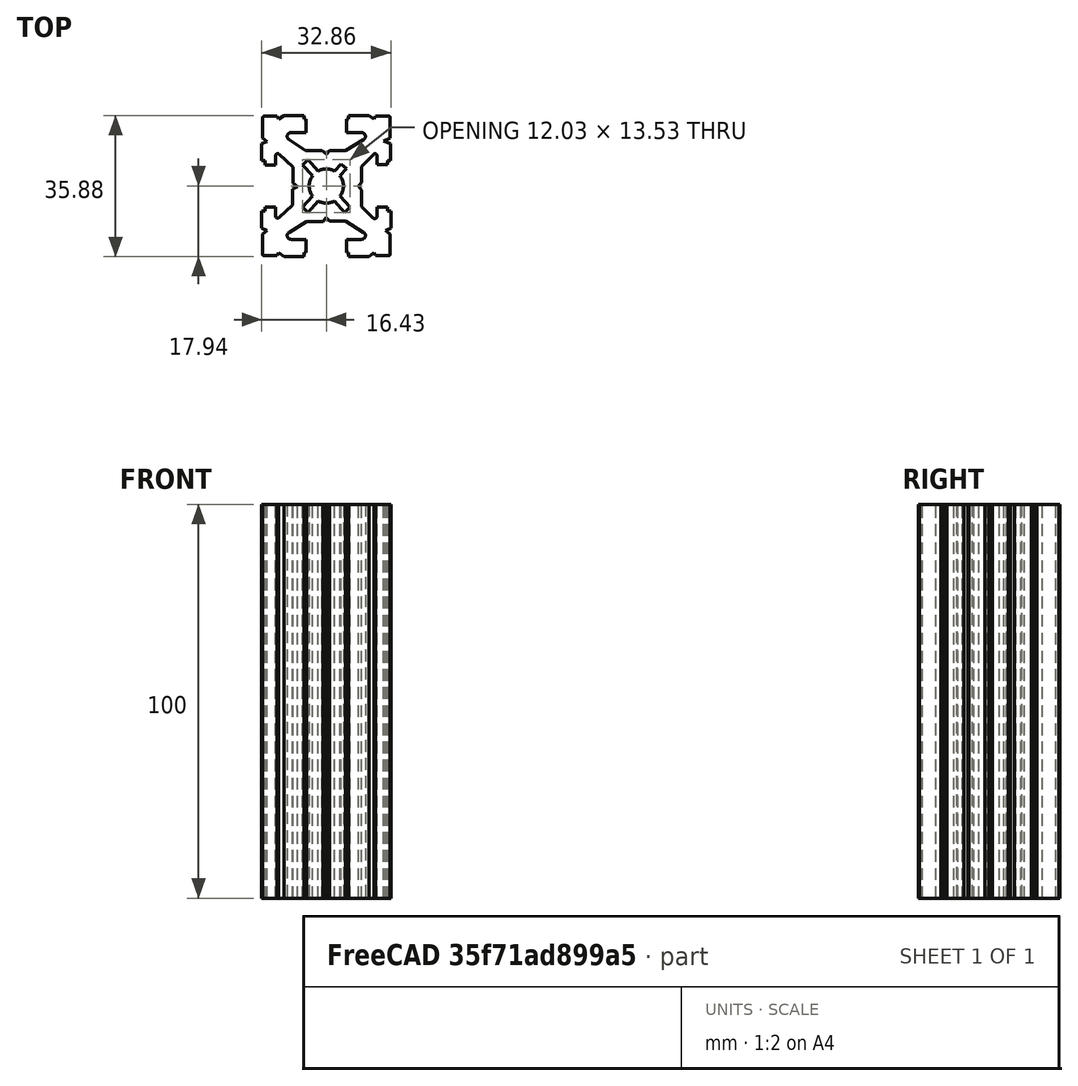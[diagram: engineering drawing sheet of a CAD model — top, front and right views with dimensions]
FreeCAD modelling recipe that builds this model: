
FCSTD DOCUMENT  (FreeCAD 0.17R13509 (Git))
Label: Profile Bosh 30x30mm
License: Creative Commons Attribution 3.0
LicenseURL: https://creativecommons.org/licenses/by/3.0/
objects: Sketcher::SketchObject×2, PartDesign::Pad×1, PartDesign::Body×1, App::Part×1
note: 5 computed .brp shape members not serialized (recipe doc carries the construction recipe); baked Part::Feature solids carry a one-line shape summary decoded from their .brp

FEATURE [Sketcher::SketchObject] Sketch
  sketch-geometry (116):
    g0: BSplineCurve PolesCount=2 KnotsCount=2 Degree=1 IsPeriodic=0
    g1: BSplineCurve PolesCount=2 KnotsCount=2 Degree=1 IsPeriodic=0
    g2: BSplineCurve PolesCount=2 KnotsCount=2 Degree=1 IsPeriodic=0
    g3: BSplineCurve PolesCount=3 KnotsCount=2 Degree=2 IsPeriodic=0
    g4: BSplineCurve PolesCount=3 KnotsCount=2 Degree=2 IsPeriodic=0
    g5: BSplineCurve PolesCount=3 KnotsCount=2 Degree=2 IsPeriodic=0
    g6: BSplineCurve PolesCount=3 KnotsCount=2 Degree=2 IsPeriodic=0
    g7: BSplineCurve PolesCount=3 KnotsCount=2 Degree=2 IsPeriodic=0
    g8: BSplineCurve PolesCount=3 KnotsCount=2 Degree=2 IsPeriodic=0
    g9: BSplineCurve PolesCount=3 KnotsCount=2 Degree=2 IsPeriodic=0
    g10: BSplineCurve PolesCount=3 KnotsCount=2 Degree=2 IsPeriodic=0
    g11: BSplineCurve PolesCount=2 KnotsCount=2 Degree=1 IsPeriodic=0
    g12: BSplineCurve PolesCount=2 KnotsCount=2 Degree=1 IsPeriodic=0
    g13: BSplineCurve PolesCount=2 KnotsCount=2 Degree=1 IsPeriodic=0
    g14: BSplineCurve PolesCount=2 KnotsCount=2 Degree=1 IsPeriodic=0
    g15: BSplineCurve PolesCount=2 KnotsCount=2 Degree=1 IsPeriodic=0
    g16: BSplineCurve PolesCount=2 KnotsCount=2 Degree=1 IsPeriodic=0
    g17: BSplineCurve PolesCount=2 KnotsCount=2 Degree=1 IsPeriodic=0
    g18: BSplineCurve PolesCount=2 KnotsCount=2 Degree=1 IsPeriodic=0
    g19: BSplineCurve PolesCount=2 KnotsCount=2 Degree=1 IsPeriodic=0
    g20: BSplineCurve PolesCount=2 KnotsCount=2 Degree=1 IsPeriodic=0
    g21: BSplineCurve PolesCount=2 KnotsCount=2 Degree=1 IsPeriodic=0
    g22: BSplineCurve PolesCount=2 KnotsCount=2 Degree=1 IsPeriodic=0
    g23: BSplineCurve PolesCount=2 KnotsCount=2 Degree=1 IsPeriodic=0
    g24: BSplineCurve PolesCount=2 KnotsCount=2 Degree=1 IsPeriodic=0
    g25: BSplineCurve PolesCount=2 KnotsCount=2 Degree=1 IsPeriodic=0
    g26: BSplineCurve PolesCount=2 KnotsCount=2 Degree=1 IsPeriodic=0
    g27: BSplineCurve PolesCount=2 KnotsCount=2 Degree=1 IsPeriodic=0
    g28: BSplineCurve PolesCount=2 KnotsCount=2 Degree=1 IsPeriodic=0
    g29: BSplineCurve PolesCount=2 KnotsCount=2 Degree=1 IsPeriodic=0
    g30: BSplineCurve PolesCount=2 KnotsCount=2 Degree=1 IsPeriodic=0
    g31: BSplineCurve PolesCount=2 KnotsCount=2 Degree=1 IsPeriodic=0
    g32: BSplineCurve PolesCount=2 KnotsCount=2 Degree=1 IsPeriodic=0
    g33: BSplineCurve PolesCount=2 KnotsCount=2 Degree=1 IsPeriodic=0
    g34: BSplineCurve PolesCount=2 KnotsCount=2 Degree=1 IsPeriodic=0
    g35: BSplineCurve PolesCount=2 KnotsCount=2 Degree=1 IsPeriodic=0
    g36: BSplineCurve PolesCount=2 KnotsCount=2 Degree=1 IsPeriodic=0
    g37: BSplineCurve PolesCount=2 KnotsCount=2 Degree=1 IsPeriodic=0
    g38: BSplineCurve PolesCount=2 KnotsCount=2 Degree=1 IsPeriodic=0
    g39: BSplineCurve PolesCount=2 KnotsCount=2 Degree=1 IsPeriodic=0
    g40: BSplineCurve PolesCount=2 KnotsCount=2 Degree=1 IsPeriodic=0
    g41: BSplineCurve PolesCount=2 KnotsCount=2 Degree=1 IsPeriodic=0
    g42: BSplineCurve PolesCount=2 KnotsCount=2 Degree=1 IsPeriodic=0
    g43: BSplineCurve PolesCount=2 KnotsCount=2 Degree=1 IsPeriodic=0
    g44: BSplineCurve PolesCount=3 KnotsCount=2 Degree=2 IsPeriodic=0
    g45: BSplineCurve PolesCount=2 KnotsCount=2 Degree=1 IsPeriodic=0
    g46: BSplineCurve PolesCount=2 KnotsCount=2 Degree=1 IsPeriodic=0
    g47: BSplineCurve PolesCount=2 KnotsCount=2 Degree=1 IsPeriodic=0
    g48: BSplineCurve PolesCount=2 KnotsCount=2 Degree=1 IsPeriodic=0
    g49: BSplineCurve PolesCount=3 KnotsCount=2 Degree=2 IsPeriodic=0
    g50: BSplineCurve PolesCount=2 KnotsCount=2 Degree=1 IsPeriodic=0
    g51: BSplineCurve PolesCount=3 KnotsCount=2 Degree=2 IsPeriodic=0
    g52: BSplineCurve PolesCount=3 KnotsCount=2 Degree=2 IsPeriodic=0
    g53: BSplineCurve PolesCount=3 KnotsCount=2 Degree=2 IsPeriodic=0
    g54: BSplineCurve PolesCount=2 KnotsCount=2 Degree=1 IsPeriodic=0
    g55: BSplineCurve PolesCount=2 KnotsCount=2 Degree=1 IsPeriodic=0
    g56: BSplineCurve PolesCount=2 KnotsCount=2 Degree=1 IsPeriodic=0
    g57: BSplineCurve PolesCount=2 KnotsCount=2 Degree=1 IsPeriodic=0
    g58: BSplineCurve PolesCount=3 KnotsCount=2 Degree=2 IsPeriodic=0
    g59: BSplineCurve PolesCount=3 KnotsCount=2 Degree=2 IsPeriodic=0
    g60: BSplineCurve PolesCount=3 KnotsCount=2 Degree=2 IsPeriodic=0
    g61: BSplineCurve PolesCount=2 KnotsCount=2 Degree=1 IsPeriodic=0
    g62: BSplineCurve PolesCount=2 KnotsCount=2 Degree=1 IsPeriodic=0
    g63: BSplineCurve PolesCount=2 KnotsCount=2 Degree=1 IsPeriodic=0
    g64: BSplineCurve PolesCount=2 KnotsCount=2 Degree=1 IsPeriodic=0
    g65: BSplineCurve PolesCount=2 KnotsCount=2 Degree=1 IsPeriodic=0
    g66: BSplineCurve PolesCount=2 KnotsCount=2 Degree=1 IsPeriodic=0
    g67: BSplineCurve PolesCount=2 KnotsCount=2 Degree=1 IsPeriodic=0
    g68: BSplineCurve PolesCount=2 KnotsCount=2 Degree=1 IsPeriodic=0
    g69: BSplineCurve PolesCount=2 KnotsCount=2 Degree=1 IsPeriodic=0
    g70: BSplineCurve PolesCount=2 KnotsCount=2 Degree=1 IsPeriodic=0
    g71: BSplineCurve PolesCount=2 KnotsCount=2 Degree=1 IsPeriodic=0
    g72: BSplineCurve PolesCount=2 KnotsCount=2 Degree=1 IsPeriodic=0
    g73: BSplineCurve PolesCount=2 KnotsCount=2 Degree=1 IsPeriodic=0
    g74: BSplineCurve PolesCount=2 KnotsCount=2 Degree=1 IsPeriodic=0
    g75: BSplineCurve PolesCount=2 KnotsCount=2 Degree=1 IsPeriodic=0
    g76: BSplineCurve PolesCount=2 KnotsCount=2 Degree=1 IsPeriodic=0
    g77: BSplineCurve PolesCount=2 KnotsCount=2 Degree=1 IsPeriodic=0
    g78: BSplineCurve PolesCount=2 KnotsCount=2 Degree=1 IsPeriodic=0
    g79: BSplineCurve PolesCount=2 KnotsCount=2 Degree=1 IsPeriodic=0
    g80: BSplineCurve PolesCount=2 KnotsCount=2 Degree=1 IsPeriodic=0
    g81: BSplineCurve PolesCount=2 KnotsCount=2 Degree=1 IsPeriodic=0
    g82: BSplineCurve PolesCount=2 KnotsCount=2 Degree=1 IsPeriodic=0
    g83: BSplineCurve PolesCount=2 KnotsCount=2 Degree=1 IsPeriodic=0
    g84: BSplineCurve PolesCount=2 KnotsCount=2 Degree=1 IsPeriodic=0
    g85: BSplineCurve PolesCount=2 KnotsCount=2 Degree=1 IsPeriodic=0
    g86: BSplineCurve PolesCount=2 KnotsCount=2 Degree=1 IsPeriodic=0
    g87: BSplineCurve PolesCount=2 KnotsCount=2 Degree=1 IsPeriodic=0
    g88: BSplineCurve PolesCount=2 KnotsCount=2 Degree=1 IsPeriodic=0
    g89: BSplineCurve PolesCount=2 KnotsCount=2 Degree=1 IsPeriodic=0
    g90: BSplineCurve PolesCount=2 KnotsCount=2 Degree=1 IsPeriodic=0
    g91: BSplineCurve PolesCount=2 KnotsCount=2 Degree=1 IsPeriodic=0
    g92: BSplineCurve PolesCount=2 KnotsCount=2 Degree=1 IsPeriodic=0
    g93: BSplineCurve PolesCount=2 KnotsCount=2 Degree=1 IsPeriodic=0
    g94: BSplineCurve PolesCount=2 KnotsCount=2 Degree=1 IsPeriodic=0
    g95: BSplineCurve PolesCount=2 KnotsCount=2 Degree=1 IsPeriodic=0
    g96: BSplineCurve PolesCount=2 KnotsCount=2 Degree=1 IsPeriodic=0
    g97: BSplineCurve PolesCount=2 KnotsCount=2 Degree=1 IsPeriodic=0
    g98: BSplineCurve PolesCount=2 KnotsCount=2 Degree=1 IsPeriodic=0
    g99: BSplineCurve PolesCount=2 KnotsCount=2 Degree=1 IsPeriodic=0
    g100: BSplineCurve PolesCount=2 KnotsCount=2 Degree=1 IsPeriodic=0
    g101: BSplineCurve PolesCount=2 KnotsCount=2 Degree=1 IsPeriodic=0
    g102: BSplineCurve PolesCount=2 KnotsCount=2 Degree=1 IsPeriodic=0
    g103: BSplineCurve PolesCount=2 KnotsCount=2 Degree=1 IsPeriodic=0
    g104: BSplineCurve PolesCount=2 KnotsCount=2 Degree=1 IsPeriodic=0
    g105: BSplineCurve PolesCount=2 KnotsCount=2 Degree=1 IsPeriodic=0
    g106: BSplineCurve PolesCount=2 KnotsCount=2 Degree=1 IsPeriodic=0
    g107: BSplineCurve PolesCount=2 KnotsCount=2 Degree=1 IsPeriodic=0
    g108: BSplineCurve PolesCount=2 KnotsCount=2 Degree=1 IsPeriodic=0
    g109: BSplineCurve PolesCount=2 KnotsCount=2 Degree=1 IsPeriodic=0
    g110: BSplineCurve PolesCount=2 KnotsCount=2 Degree=1 IsPeriodic=0
    g111: BSplineCurve PolesCount=2 KnotsCount=2 Degree=1 IsPeriodic=0
    g112: BSplineCurve PolesCount=2 KnotsCount=2 Degree=1 IsPeriodic=0
    g113: BSplineCurve PolesCount=2 KnotsCount=2 Degree=1 IsPeriodic=0
    g114: BSplineCurve PolesCount=2 KnotsCount=2 Degree=1 IsPeriodic=0
    g115: BSplineCurve PolesCount=2 KnotsCount=2 Degree=1 IsPeriodic=0
FEATURE [Sketcher::SketchObject] Sketch001
  MapMode = 5
  Support = -> [XY_Plane001]
  sketch-geometry (121):
    g0: LineSegment [constr] StartX=0 StartY=0 StartZ=0 EndX=0 EndY=8.13256 EndZ=0
    g1: LineSegment [constr] StartX=8.13256 StartY=0 StartZ=0 EndX=0 EndY=0 EndZ=0
    g2: LineSegment StartX=0 StartY=8.13256 StartZ=0 EndX=0.863984 EndY=8.96505 EndZ=0
    g3: LineSegment StartX=0.863984 StartY=8.96505 StartZ=0 EndX=4.93425 EndY=8.96505 EndZ=0
    g4: LineSegment StartX=4.93425 StartY=8.96505 StartZ=0 EndX=9.48637 EndY=11.797 EndZ=0
    g5: LineSegment StartX=8.98459 StartY=13.5535 StartZ=0 EndX=5.15812 EndY=13.5535 EndZ=0
    g6: LineSegment StartX=5.15812 StartY=13.5535 StartZ=0 EndX=5.15812 EndY=16.9407 EndZ=0
    g7: LineSegment StartX=5.15812 StartY=16.9407 StartZ=0 EndX=5.6531 EndY=16.9407 EndZ=0
    g8: LineSegment StartX=5.6531 StartY=16.9407 StartZ=0 EndX=5.6531 EndY=17.9363 EndZ=0
    g9: LineSegment StartX=5.6531 StartY=17.9363 StartZ=0 EndX=10.7923 EndY=17.9363 EndZ=0
    g10: LineSegment StartX=10.7923 StartY=17.9363 StartZ=0 EndX=12.0719 EndY=16.9647 EndZ=0
    g11: LineSegment StartX=12.0719 StartY=16.9647 StartZ=0 EndX=12.5221 EndY=17.7592 EndZ=0
    g12: LineSegment StartX=12.5221 StartY=17.7592 StartZ=0 EndX=15.8708 EndY=17.7592 EndZ=0
    g13: LineSegment StartX=16.246 StartY=17.384 StartZ=0 EndX=16.246 EndY=12.1724 EndZ=0
    g14: LineSegment StartX=16.246 StartY=12.1724 StartZ=0 EndX=14.4892 EndY=11.3845 EndZ=0
    g15: LineSegment StartX=14.4892 StartY=11.3845 StartZ=0 EndX=16.2567 EndY=10.735 EndZ=0
    g16: LineSegment StartX=16.2567 StartY=10.735 StartZ=0 EndX=16.2567 EndY=6.42108 EndZ=0
    g17: LineSegment StartX=16.2567 StartY=6.42108 StartZ=0 EndX=15.6194 EndY=6.42108 EndZ=0
    g18: ArcOfCircle CenterX=15.8708 CenterY=17.384 CenterZ=0 NormalX=0 NormalY=0 NormalZ=1 AngleXU=0 Radius=0.375206 StartAngle=0 EndAngle=1.5708
    g19: ArcOfCircle CenterX=12.38 CenterY=7.66792 CenterZ=0 NormalX=0 NormalY=0 NormalZ=1 AngleXU=0 Radius=0.511001 StartAngle=0 EndAngle=2.35619
    g20: ArcOfCircle CenterX=8.98459 CenterY=12.6036 CenterZ=0 NormalX=0 NormalY=0 NormalZ=1 AngleXU=0 Radius=0.949916 StartAngle=5.26891 EndAngle=7.85398
    g21: LineSegment StartX=15.6194 StartY=6.42108 StartZ=0 EndX=15.6194 EndY=5.37886 EndZ=0
    g22: LineSegment StartX=15.6194 StartY=5.37886 StartZ=0 EndX=12.891 EndY=5.37886 EndZ=0
    g23: LineSegment StartX=12.891 StartY=5.37886 StartZ=0 EndX=12.891 EndY=7.66792 EndZ=0
    g24: LineSegment StartX=12.0187 StartY=8.02925 StartZ=0 EndX=8.94375 EndY=4.95429 EndZ=0
    g25: LineSegment StartX=8.94375 StartY=4.95429 StartZ=0 EndX=8.94375 EndY=0.884017 EndZ=0
    g26: LineSegment StartX=8.94375 StartY=0.884017 StartZ=0 EndX=8.13256 EndY=0 EndZ=0
    g27: ArcOfCircle CenterX=0 CenterY=0 CenterZ=0 NormalX=0 NormalY=0 NormalZ=1 AngleXU=0 Radius=4.34461 StartAngle=1.06729 EndAngle=2.0743
    g28: LineSegment StartX=-2.09626 StartY=3.80544 StartZ=0 EndX=-4.58638 EndY=6.76319 EndZ=0
    g29: LineSegment StartX=-4.58638 StartY=6.76319 StartZ=0 EndX=-6.01301 EndY=5.3625 EndZ=0
    g30: LineSegment StartX=-6.01301 StartY=5.3625 StartZ=0 EndX=-3.47101 EndY=2.61299 EndZ=0
    g31: LineSegment StartX=2.09626 StartY=3.80544 StartZ=0 EndX=3.70713 EndY=5.62355 EndZ=0
    g32: LineSegment StartX=3.70713 StartY=5.62355 StartZ=0 EndX=5.08583 EndY=4.45696 EndZ=0
    g33: LineSegment StartX=5.08583 StartY=4.45696 StartZ=0 EndX=3.47101 EndY=2.61299 EndZ=0
    g34: LineSegment StartX=2.09626 StartY=-3.80544 StartZ=0 EndX=4.58638 EndY=-6.76319 EndZ=0
    g35: LineSegment StartX=4.58638 StartY=-6.76319 StartZ=0 EndX=6.01301 EndY=-5.3625 EndZ=0
    g36: LineSegment StartX=6.01301 StartY=-5.3625 StartZ=0 EndX=3.47101 EndY=-2.61299 EndZ=0
    g37: LineSegment StartX=-2.09626 StartY=-3.80544 StartZ=0 EndX=-4.58638 EndY=-6.76319 EndZ=0
    g38: LineSegment StartX=-6.01301 StartY=-5.3625 StartZ=0 EndX=-3.47101 EndY=-2.61299 EndZ=0
    g39: LineSegment StartX=-4.58638 StartY=-6.76319 StartZ=0 EndX=-6.01301 EndY=-5.3625 EndZ=0
    g40: ArcOfCircle CenterX=0 CenterY=0 CenterZ=0 NormalX=0 NormalY=0 NormalZ=1 AngleXU=0 Radius=4.34461 StartAngle=2.4963 EndAngle=3.78689
    g41: ArcOfCircle CenterX=0 CenterY=0 CenterZ=0 NormalX=0 NormalY=0 NormalZ=1 AngleXU=0 Radius=4.34461 StartAngle=4.20889 EndAngle=5.21589
    g42: ArcOfCircle CenterX=0 CenterY=0 CenterZ=0 NormalX=0 NormalY=0 NormalZ=1 AngleXU=0 Radius=4.34461 StartAngle=5.63789 EndAngle=6.92848
    g43: LineSegment [constr] StartX=8.94375 StartY=4.95429 StartZ=0 EndX=10.2141 EndY=4.95429 EndZ=0
    g44: LineSegment StartX=0 StartY=8.13256 StartZ=0 EndX=-1.12485 EndY=9.01316 EndZ=0
    g45: LineSegment StartX=-1.12485 StartY=9.01316 StartZ=0 EndX=-5.23766 EndY=9.01316 EndZ=0
    g46: LineSegment StartX=-5.23766 StartY=9.01316 StartZ=0 EndX=-9.50558 EndY=11.8091 EndZ=0
    g47: LineSegment StartX=-8.98499 StartY=13.5537 StartZ=0 EndX=-5.15812 EndY=13.5537 EndZ=0
    g48: LineSegment StartX=-5.15812 StartY=13.5537 StartZ=0 EndX=-5.15812 EndY=16.9407 EndZ=0
    g49: LineSegment StartX=-5.15812 StartY=16.9407 StartZ=0 EndX=-5.6531 EndY=16.9407 EndZ=0
    g50: LineSegment StartX=-5.6531 StartY=16.9407 StartZ=0 EndX=-5.6531 EndY=17.9363 EndZ=0
    g51: LineSegment StartX=-5.6531 StartY=17.9363 StartZ=0 EndX=-10.7923 EndY=17.9363 EndZ=0
    g52: LineSegment StartX=-10.7923 StartY=17.9363 StartZ=0 EndX=-12.0719 EndY=16.9647 EndZ=0
    g53: LineSegment StartX=-12.0719 StartY=16.9647 StartZ=0 EndX=-12.5221 EndY=17.7251 EndZ=0
    g54: LineSegment StartX=-12.5221 StartY=17.7251 StartZ=0 EndX=-15.8282 EndY=17.7251 EndZ=0
    g55: LineSegment StartX=-16.1524 StartY=17.401 StartZ=0 EndX=-16.1524 EndY=12.1805 EndZ=0
    g56: LineSegment StartX=-16.1524 StartY=12.1805 StartZ=0 EndX=-14.9921 EndY=11.3367 EndZ=0
    g57: LineSegment StartX=-14.9921 StartY=11.3367 StartZ=0 EndX=-16.4328 EndY=10.7136 EndZ=0
    g58: LineSegment StartX=-16.4328 StartY=10.7136 StartZ=0 EndX=-16.4328 EndY=6.42108 EndZ=0
    g59: LineSegment StartX=-16.4328 StartY=6.42108 StartZ=0 EndX=-15.6194 EndY=6.42108 EndZ=0
    g60: ArcOfCircle CenterX=-15.8282 CenterY=17.401 CenterZ=0 NormalX=0 NormalY=0 NormalZ=1 AngleXU=0 Radius=0.324122 StartAngle=1.5708 EndAngle=3.14159
    g61: ArcOfCircle CenterX=-8.98499 CenterY=12.6037 CenterZ=0 NormalX=0 NormalY=0 NormalZ=1 AngleXU=0 Radius=0.949992 StartAngle=1.5708 EndAngle=4.13243
    g62: LineSegment StartX=-15.6194 StartY=6.42108 StartZ=0 EndX=-15.6194 EndY=5.3545 EndZ=0
    g63: LineSegment StartX=-15.6194 StartY=5.3545 StartZ=0 EndX=-12.8911 EndY=5.3545 EndZ=0
    g64: ArcOfCircle CenterX=-12.3588 CenterY=7.67266 CenterZ=0 NormalX=0 NormalY=0 NormalZ=1 AngleXU=0 Radius=0.532302 StartAngle=0.822691 EndAngle=3.14117
    g65: LineSegment StartX=-11.9967 StartY=8.06282 StartZ=0 EndX=-8.50501 EndY=4.82235 EndZ=0
    g66: LineSegment StartX=-8.50501 StartY=4.82235 StartZ=0 EndX=-8.50501 EndY=0.709539 EndZ=0
    g67: LineSegment StartX=-8.50501 StartY=0.709539 StartZ=0 EndX=-7.362 EndY=-0.147361 EndZ=0
    g68: LineSegment [constr] StartX=-0.0366578 StartY=0 StartZ=0 EndX=-0.0366578 EndY=-7.97192 EndZ=0
    g69: LineSegment StartX=-0.0366578 StartY=-7.97192 StartZ=0 EndX=0.851967 EndY=-8.95417 EndZ=0
    g70: LineSegment StartX=0.851967 StartY=-8.95417 StartZ=0 EndX=4.95077 EndY=-8.95417 EndZ=0
    g71: LineSegment StartX=4.95077 StartY=-8.95417 StartZ=0 EndX=9.48868 EndY=-11.7973 EndZ=0
    g72: LineSegment StartX=8.98403 StartY=-13.5532 StartZ=0 EndX=5.15812 EndY=-13.5532 EndZ=0
    g73: LineSegment StartX=5.15812 StartY=-13.5532 StartZ=0 EndX=5.15812 EndY=-16.9407 EndZ=0
    g74: LineSegment StartX=5.15812 StartY=-16.9407 StartZ=0 EndX=5.6531 EndY=-16.9407 EndZ=0
    g75: LineSegment StartX=5.6531 StartY=-16.9407 StartZ=0 EndX=5.6531 EndY=-17.9363 EndZ=0
    g76: LineSegment StartX=5.6531 StartY=-17.9363 StartZ=0 EndX=10.7923 EndY=-17.9363 EndZ=0
    g77: LineSegment StartX=10.7923 StartY=-17.9363 StartZ=0 EndX=12.0719 EndY=-16.9647 EndZ=0
    g78: LineSegment StartX=12.0719 StartY=-16.9647 StartZ=0 EndX=12.5221 EndY=-17.7251 EndZ=0
    g79: LineSegment StartX=12.5221 StartY=-17.7251 StartZ=0 EndX=15.8282 EndY=-17.7251 EndZ=0
    g80: LineSegment StartX=16.1524 StartY=-17.401 StartZ=0 EndX=16.1524 EndY=-12.1805 EndZ=0
    g81: LineSegment StartX=16.1524 StartY=-12.1805 StartZ=0 EndX=14.9921 EndY=-11.3367 EndZ=0
    g82: LineSegment StartX=14.9921 StartY=-11.3367 StartZ=0 EndX=16.4328 EndY=-10.7136 EndZ=0
    g83: LineSegment StartX=16.4328 StartY=-10.7136 StartZ=0 EndX=16.4328 EndY=-6.42108 EndZ=0
    g84: ArcOfCircle CenterX=15.8282 CenterY=-17.401 CenterZ=0 NormalX=0 NormalY=0 NormalZ=1 AngleXU=0 Radius=0.324122 StartAngle=4.71239 EndAngle=6.28319
    g85: ArcOfCircle CenterX=12.2781 CenterY=-7.67162 CenterZ=0 NormalX=0 NormalY=0 NormalZ=1 AngleXU=0 Radius=0.613906 StartAngle=3.92699 EndAngle=6.28319
    g86: ArcOfCircle CenterX=8.98403 CenterY=-12.6027 CenterZ=0 NormalX=0 NormalY=0 NormalZ=1 AngleXU=0 Radius=0.950502 StartAngle=4.71239 EndAngle=7.29429
    g87: LineSegment StartX=12.892 StartY=-5.37886 StartZ=0 EndX=12.892 EndY=-7.67162 EndZ=0
    g88: LineSegment StartX=11.844 StartY=-8.10572 StartZ=0 EndX=8.9097 EndY=-5.17142 EndZ=0
    g89: LineSegment StartX=-0.0366578 StartY=-7.97192 StartZ=0 EndX=-0.845387 EndY=-8.98483 EndZ=0
    g90: LineSegment StartX=-0.845387 StartY=-8.98483 StartZ=0 EndX=-4.96492 EndY=-8.98483 EndZ=0
    g91: LineSegment StartX=-4.96492 StartY=-8.98483 StartZ=0 EndX=-9.48593 EndY=-11.7955 EndZ=0
    g92: LineSegment StartX=-8.98406 StartY=-13.5533 StartZ=0 EndX=-5.15812 EndY=-13.5533 EndZ=0
    g93: LineSegment StartX=-5.15812 StartY=-13.5533 StartZ=0 EndX=-5.15812 EndY=-16.9407 EndZ=0
    g94: LineSegment StartX=-5.15812 StartY=-16.9407 StartZ=0 EndX=-5.6531 EndY=-16.9407 EndZ=0
    g95: LineSegment StartX=-5.6531 StartY=-16.9407 StartZ=0 EndX=-5.6531 EndY=-17.9363 EndZ=0
    g96: LineSegment StartX=-5.6531 StartY=-17.9363 StartZ=0 EndX=-10.7923 EndY=-17.9363 EndZ=0
    g97: LineSegment StartX=-10.7923 StartY=-17.9363 StartZ=0 EndX=-12.0719 EndY=-16.9647 EndZ=0
    g98: LineSegment StartX=-12.0719 StartY=-16.9647 StartZ=0 EndX=-12.5221 EndY=-17.7251 EndZ=0
    g99: LineSegment StartX=-12.5221 StartY=-17.7251 StartZ=0 EndX=-15.8282 EndY=-17.7251 EndZ=0
    g100: LineSegment StartX=-16.1524 StartY=-17.401 StartZ=0 EndX=-16.1524 EndY=-12.1805 EndZ=0
    g101: LineSegment StartX=-16.1524 StartY=-12.1805 StartZ=0 EndX=-14.9921 EndY=-11.3367 EndZ=0
    g102: LineSegment StartX=-14.9921 StartY=-11.3367 StartZ=0 EndX=-16.4328 EndY=-10.7136 EndZ=0
    g103: LineSegment StartX=-16.4328 StartY=-10.7136 StartZ=0 EndX=-16.4328 EndY=-6.42108 EndZ=0
    g104: ArcOfCircle CenterX=-15.8282 CenterY=-17.401 CenterZ=0 NormalX=0 NormalY=0 NormalZ=1 AngleXU=0 Radius=0.324122 StartAngle=3.14159 EndAngle=4.71239
    g105: ArcOfCircle CenterX=-8.98406 CenterY=-12.6028 CenterZ=0 NormalX=0 NormalY=0 NormalZ=1 AngleXU=0 Radius=0.950558 StartAngle=2.12701 EndAngle=4.71239
    g106: ArcOfCircle CenterX=-12.3712 CenterY=-7.67362 CenterZ=0 NormalX=0 NormalY=0 NormalZ=1 AngleXU=0 Radius=0.522418 StartAngle=3.14233 EndAngle=5.45425
    g107: LineSegment StartX=-12.0182 StartY=-8.05875 StartZ=0 EndX=-8.51881 EndY=-4.85154 EndZ=0
    g108: LineSegment StartX=16.4328 StartY=-6.42108 StartZ=0 EndX=15.6194 EndY=-6.42108 EndZ=0
    g109: LineSegment StartX=15.6194 StartY=-6.42108 StartZ=0 EndX=15.6194 EndY=-5.37886 EndZ=0
    g110: LineSegment StartX=15.6194 StartY=-5.37886 StartZ=0 EndX=12.892 EndY=-5.37886 EndZ=0
    g111: LineSegment StartX=8.9097 StartY=-5.17142 StartZ=0 EndX=8.9097 EndY=-1.07262 EndZ=0
    g112: LineSegment StartX=8.9097 StartY=-1.07262 StartZ=0 EndX=8.13256 EndY=0 EndZ=0
    g113: LineSegment [constr] StartX=8.9097 StartY=-5.17142 StartZ=0 EndX=10.2141 EndY=-5.17142 EndZ=0
    g114: LineSegment StartX=-16.4328 StartY=-6.42108 StartZ=0 EndX=-15.6194 EndY=-6.42108 EndZ=0
    g115: LineSegment StartX=-15.6194 StartY=-6.42108 StartZ=0 EndX=-15.6194 EndY=-5.37886 EndZ=0
    g116: LineSegment StartX=-15.6194 StartY=-5.37886 StartZ=0 EndX=-12.8936 EndY=-5.37886 EndZ=0
    g117: LineSegment StartX=-8.51881 StartY=-4.85154 StartZ=0 EndX=-8.51881 EndY=-0.732016 EndZ=0
    g118: LineSegment StartX=-8.51881 StartY=-0.732016 StartZ=0 EndX=-7.362 EndY=-0.147361 EndZ=0
    g119: LineSegment StartX=-12.8911 StartY=7.67288 StartZ=0 EndX=-12.8911 EndY=5.3545 EndZ=0
    g120: LineSegment StartX=-12.8936 StartY=-5.37886 StartZ=0 EndX=-12.8936 EndY=-7.674 EndZ=0
  constraints (200):
    c: PointOnObject(g0,g-2)
    c: Coincident(g-1,g0)
    c: Coincident(g1,g0)
    c: Horizontal(g1)
    c: Equal(g1,g0)
    c: Coincident(g2,g3)
    c: Horizontal(g3)
    c: Coincident(g3,g4)
    c: Horizontal(g5)
    c: Coincident(g5,g6)
    c: Vertical(g6)
    c: Coincident(g6,g7)
    c: Horizontal(g7)
    c: Coincident(g7,g8)
    c: Coincident(g8,g9)
    c: Horizontal(g9)
    c: Coincident(g9,g10)
    c: Coincident(g10,g11)
    c: Coincident(g11,g12)
    c: Horizontal(g12)
    c: Vertical(g13)
    c: Coincident(g13,g14)
    c: Coincident(g14,g15)
    c: Coincident(g15,g16)
    c: Vertical(g16)
    c: Coincident(g16,g17)
    c: Horizontal(g17)
    c: Coincident(g17,g21)
    c: Coincident(g21,g22)
    c: Horizontal(g22)
    c: Coincident(g22,g23)
    c: Vertical(g23)
    c: Coincident(g24,g25)
    c: Vertical(g25)
    c: Coincident(g25,g26)
    c: Tangent(g12,g18) = 1.5708
    c: Tangent(g13,g18) = 1.5708
    c: Tangent(g23,g19) = -1.5708
    c: Tangent(g24,g19) = -1.5708
    c: Tangent(g4,g20) = -1.5708
    c: Tangent(g5,g20) = -1.5708
    c: Coincident(g1,g26)
    c: Vertical(g8)
    c: Coincident(g27,g-1)
    c: Coincident(g31,g32)
    c: Coincident(g32,g33)
    c: Coincident(g34,g35)
    c: Coincident(g35,g36)
    c: PointOnObject(g38,g27)
    c: PointOnObject(g37,g27)
    c: PointOnObject(g34,g27)
    c: PointOnObject(g36,g27)
    c: Coincident(g27,g31)
    c: Coincident(g42,g33)
    c: Equal(g27,g40)
    c: Coincident(g27,g40)
    c: Equal(g40,g41)
    c: PointOnObject(g40,g38)
    c: PointOnObject(g41,g37)
    c: Coincident(g40,g41)
    c: Equal(g41,g42)
    c: PointOnObject(g41,g34)
    c: PointOnObject(g42,g36)
    c: Coincident(g41,g42)
    c: Vertical(g21)
    c: Coincident(g24,g43)
    c: Horizontal(g43)
    c: Angle(g43,g24) = 0.785398
    c: Coincident(g0,g2)
    c: Equal(g25,g3)
    c: Equal(g26,g2)
    c: Coincident(g44,g45)
    c: Horizontal(g45)
    c: Coincident(g45,g46)
    c: Horizontal(g47)
    c: Coincident(g47,g48)
    c: Vertical(g48)
    c: Coincident(g48,g49)
    c: Horizontal(g49)
    c: Coincident(g49,g50)
    c: Coincident(g50,g51)
    c: Horizontal(g51)
    c: Coincident(g51,g52)
    c: Coincident(g52,g53)
    c: Coincident(g53,g54)
    c: Horizontal(g54)
    c: Vertical(g55)
    c: Coincident(g55,g56)
    c: Coincident(g56,g57)
    c: Coincident(g57,g58)
    c: Vertical(g58)
    c: Coincident(g58,g59)
    c: Horizontal(g59)
    c: Coincident(g59,g62)
    c: Coincident(g62,g63)
    c: Horizontal(g63)
    c: Coincident(g65,g66)
    c: Vertical(g66)
    c: Coincident(g66,g67)
    c: Tangent(g54,g60) = -1.5708
    c: Tangent(g55,g60) = -1.5708
    c: Tangent(g65,g64) = 1.5708
    c: Tangent(g46,g61) = 1.5708
    c: Tangent(g47,g61) = 1.5708
    c: Vertical(g50)
    c: Vertical(g62)
    c: Equal(g66,g45)
    c: Equal(g67,g44)
    c: Coincident(g44,g0)
    c: Coincident(g69,g70)
    c: Horizontal(g70)
    c: Coincident(g70,g71)
    c: Horizontal(g72)
    c: Coincident(g72,g73)
    c: Vertical(g73)
    c: Coincident(g73,g74)
    c: Horizontal(g74)
    c: Coincident(g74,g75)
    c: Coincident(g75,g76)
    c: Horizontal(g76)
    c: Coincident(g76,g77)
    c: Coincident(g77,g78)
    c: Coincident(g78,g79)
    c: Horizontal(g79)
    c: Vertical(g80)
    c: Coincident(g80,g81)
    c: Coincident(g81,g82)
    c: Coincident(g82,g83)
    c: Vertical(g83)
    c: Coincident(g83,g108)
    c: Horizontal(g108)
    c: Coincident(g108,g109)
    c: Coincident(g109,g110)
    c: Horizontal(g110)
    c: Coincident(g110,g87)
    c: Vertical(g87)
    c: Coincident(g88,g111)
    c: Vertical(g111)
    c: Coincident(g111,g112)
    c: Tangent(g79,g84) = -1.5708
    c: Tangent(g80,g84) = -1.5708
    c: Tangent(g87,g85) = 1.5708
    c: Tangent(g88,g85) = 1.5708
    c: Tangent(g71,g86) = 1.5708
    c: Tangent(g72,g86) = 1.5708
    c: Vertical(g75)
    c: Vertical(g109)
    c: Coincident(g88,g113)
    c: Horizontal(g113)
    c: Angle(g113,g88) = -0.785398
    c: Coincident(g68,g69)
    c: Equal(g111,g70)
    c: Equal(g112,g69)
    c: Coincident(g89,g90)
    c: Horizontal(g90)
    c: Coincident(g90,g91)
    c: Horizontal(g92)
    c: Coincident(g92,g93)
    c: Vertical(g93)
    c: Coincident(g93,g94)
    c: Horizontal(g94)
    c: Coincident(g94,g95)
    c: Coincident(g95,g96)
    c: Horizontal(g96)
    c: Coincident(g96,g97)
    c: Coincident(g97,g98)
    c: Coincident(g98,g99)
    c: Horizontal(g99)
    c: Vertical(g100)
    c: Coincident(g100,g101)
    c: Coincident(g101,g102)
    c: Coincident(g102,g103)
    c: Vertical(g103)
    c: Coincident(g103,g114)
    c: Horizontal(g114)
    c: Coincident(g114,g115)
    c: Coincident(g115,g116)
    c: Horizontal(g116)
    c: Coincident(g107,g117)
    c: Vertical(g117)
    c: Coincident(g117,g118)
    c: Tangent(g99,g104) = 1.5708
    c: Tangent(g100,g104) = 1.5708
    c: Tangent(g107,g106) = -1.5708
    c: Tangent(g91,g105) = -1.5708
    c: Tangent(g92,g105) = -1.5708
    c: Vertical(g95)
    c: Vertical(g115)
    c: Equal(g117,g90)
    c: Equal(g118,g89)
    c: Coincident(g89,g68)
    c: Coincident(g112,g1)
    c: Coincident(g67,g118)
    c: Vertical(g68)
    c: Coincident(g119,g63)
    c: Vertical(g119)
    c: Coincident(g119,g64)
    c: Coincident(g116,g120)
    c: Coincident(g120,g106)
    c: Vertical(g120)
FEATURE [PartDesign::Pad] Pad
  Length = 100
  Length2 = 100
  Profile = -> Sketch001
  Refine = true
  Type = 0
FEATURE [PartDesign::Body] Body
  Group = -> [Sketch001,Pad]
  Origin = -> Origin001
  Tip = -> Pad
FEATURE [App::Part] Part
  Group = -> [Body]
  License = Creative Commons Attribution 3.0
  LicenseURL = https://creativecommons.org/licenses/by/3.0/
  Origin = -> Origin
